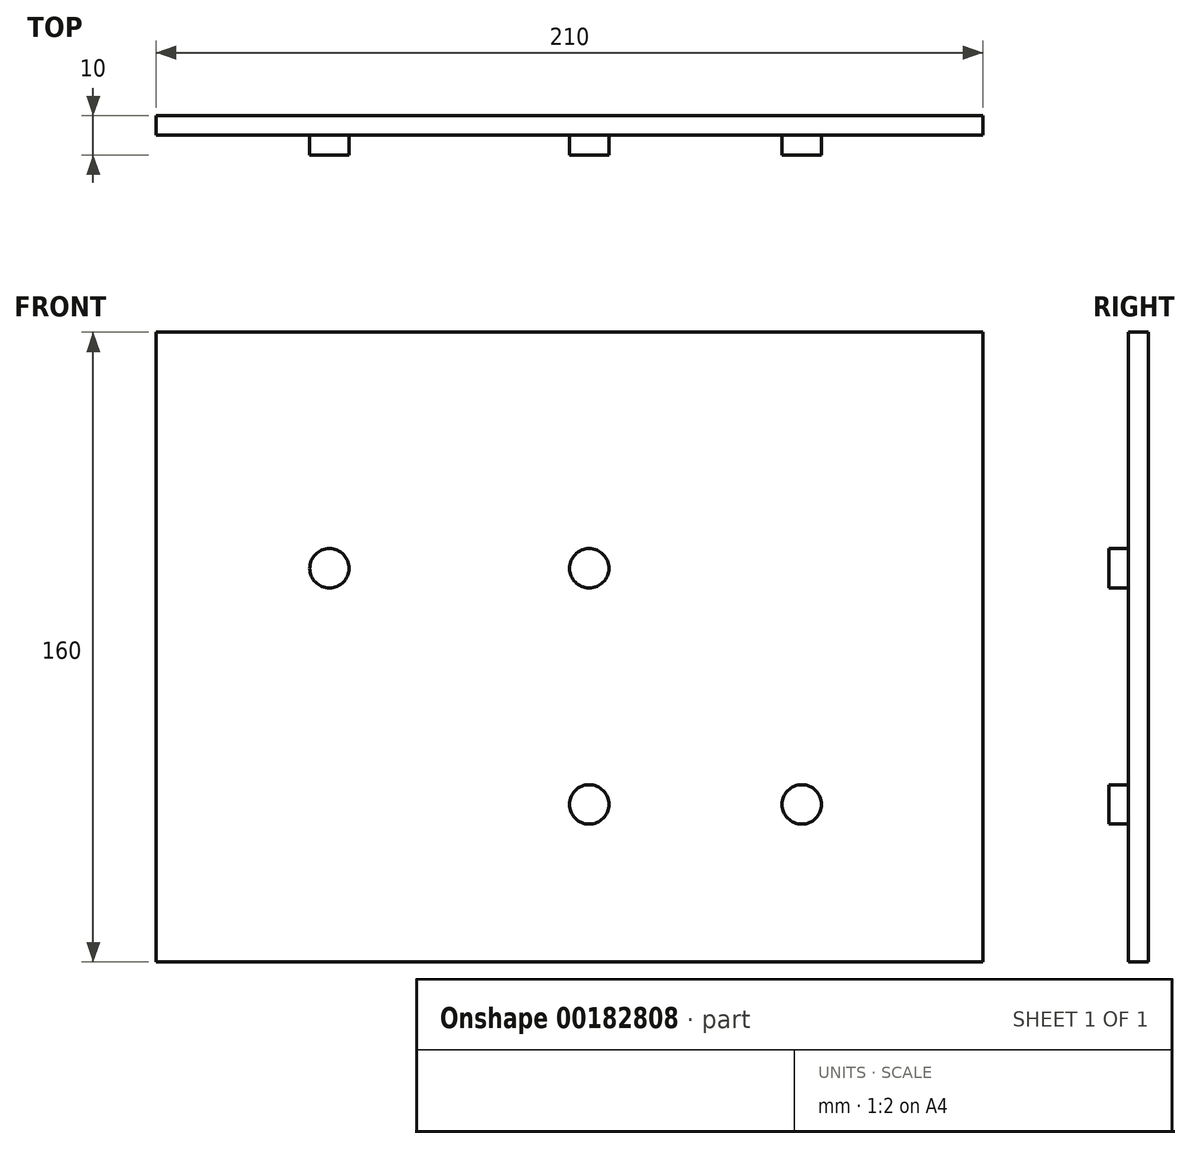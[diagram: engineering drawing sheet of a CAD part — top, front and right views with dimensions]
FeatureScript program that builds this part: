
annotation { "Feature Type Name" : "Feature", "Feature Type Description" : "" }
export const myFeature = defineFeature(function(context is Context, id is Id, definition is map)
    precondition{}
    {
        {
            var Q0;
            Q0=qCreatedBy(makeId("Front.planeOp"),FACE);
            var sketch = newSketch(context, id + "F0", { "sketchPlane" : qUnion([Q0])});
            skLineSegment(sketch, "E0.bottom", {"start": v(-110, 60) * mm, "end": v(100, 60) * mm});
            skLineSegment(sketch, "E0.top", {"start": v(-110, -100) * mm, "end": v(100, -100) * mm});
            skLineSegment(sketch, "E0.left", {"start": v(-110, 60) * mm, "end": v(-110, -100) * mm});
            skLineSegment(sketch, "E0.right", {"start": v(100, 60) * mm, "end": v(100, -100) * mm});
            skSolve(sketch);
        }
        {
            var Q0;
            Q0=makeQuery(id+"F0.imprint","IMPRINT",FACE,{"disambiguationData":[TD([[makeQuery(id+"F0.imprint","IMPRINT",EDGE,{"derivedFrom":sQuery(id+"F0.wireOp",EDGE,"E0.bottom")}),-1.0]])]});
            extrude(context, id + "F1", {"entities" : qUnion([Q0]), "depth" : 5 * mm});
        }
        {
            var Q0;
            Q0=makeQuery(id+"F1.opExtrude","CAP_FACE",FACE,{"disambiguationData":[OSD([sQuery(id+"F0.wireOp",EDGE,"E0.bottom"),sQuery(id+"F0.wireOp",EDGE,"E0.top"),sQuery(id+"F0.wireOp",EDGE,"E0.left"),sQuery(id+"F0.wireOp",EDGE,"E0.right")])],"isStart":false});
            var sketch = newSketch(context, id + "F2", { "sketchPlane" : qUnion([Q0])});
            skCircle(sketch, "E1", {"center": v(0, 0) * mm, "radius": 5 * mm});
            skCircle(sketch, "E2", {"center": v(0, -60) * mm, "radius": 5 * mm});
            skCircle(sketch, "E3", {"center": v(54, -60) * mm, "radius": 5 * mm});
            skCircle(sketch, "E4", {"center": v(-66, 0) * mm, "radius": 5 * mm});
            skSolve(sketch);
        }
        {
            var Q0;
            Q0 = qSketchRegion(id + "F2", true);
            extrude(context, id + "F3", {"entities" : qUnion([Q0]), "operationType" : NewBodyOperationType.ADD, "depth" : 5 * mm});
        }
    });
